# Revit family: CAYLEE CATERPILLAR
name_source: partatom
category: Furniture Systems
units: mm (PartAtom-declared; Revit-internal decimal feet)

## family parameters
Always vertical = Yes
Cut with Voids When Loaded = No
Part Type = Normal
Room Calculation Point = No
Round Connector Dimension = Use Diameter
Shared = No
Work Plane-Based = No

## types (1)
- CAYLEE CATERPILLAR
    BASE = Yes
    Base = <By Category>
    CAYLEE Face_1B = Black
    CAYLEE Face_1BLUE = 1BL
    CAYLEE Face_1R = E-RED
    CAYLEE Face_2W = WHITE
    Cresent Ottoman Model Number = F003-18x18
    Cresent-1 Seat Fabric = <By Category>
    Cresent-1 Side Fabric = <By Category>
    Cresent-2 Seat Fabric = <By Category>
    Cresent-2 Side Fabric = <By Category>
    Cresent-3 Seat Fabric = <By Category>
    Cresent-3 Side Fabric = <By Category>
    Cresent-4 Seat Fabric = <By Category>
    Cresent-4 Side Fabric = <By Category>
    Cresent-5 Seat Fabric = <By Category>
    Cresent-5 Side Fabric = <By Category>
    Cresent-6 Seat Fabric = <By Category>
    Cresent-6 Side Fabric = <By Category>
    Cresent-7 Seat Fabric = <By Category>
    Cresent-7 Side Fabric = <By Category>
    Description = Combo Products - CAYLEE CATERPILLAR
    G1 = Yes
    Glide = <By Category>
    Manufacturer = FOMCORE
    Model = CAYLEE CATERPILLAR
    Ottoman Seat Fabric = <By Category>
    Ottoman Side Fabric = <By Category>
    Round Ottoman with Caylee Face Model Number = F005-22x18
    URL = https://fomcore.com

## geometry (parser evidence)
native form markers: Sweep x2
no freeform markers — native parametric forms only
